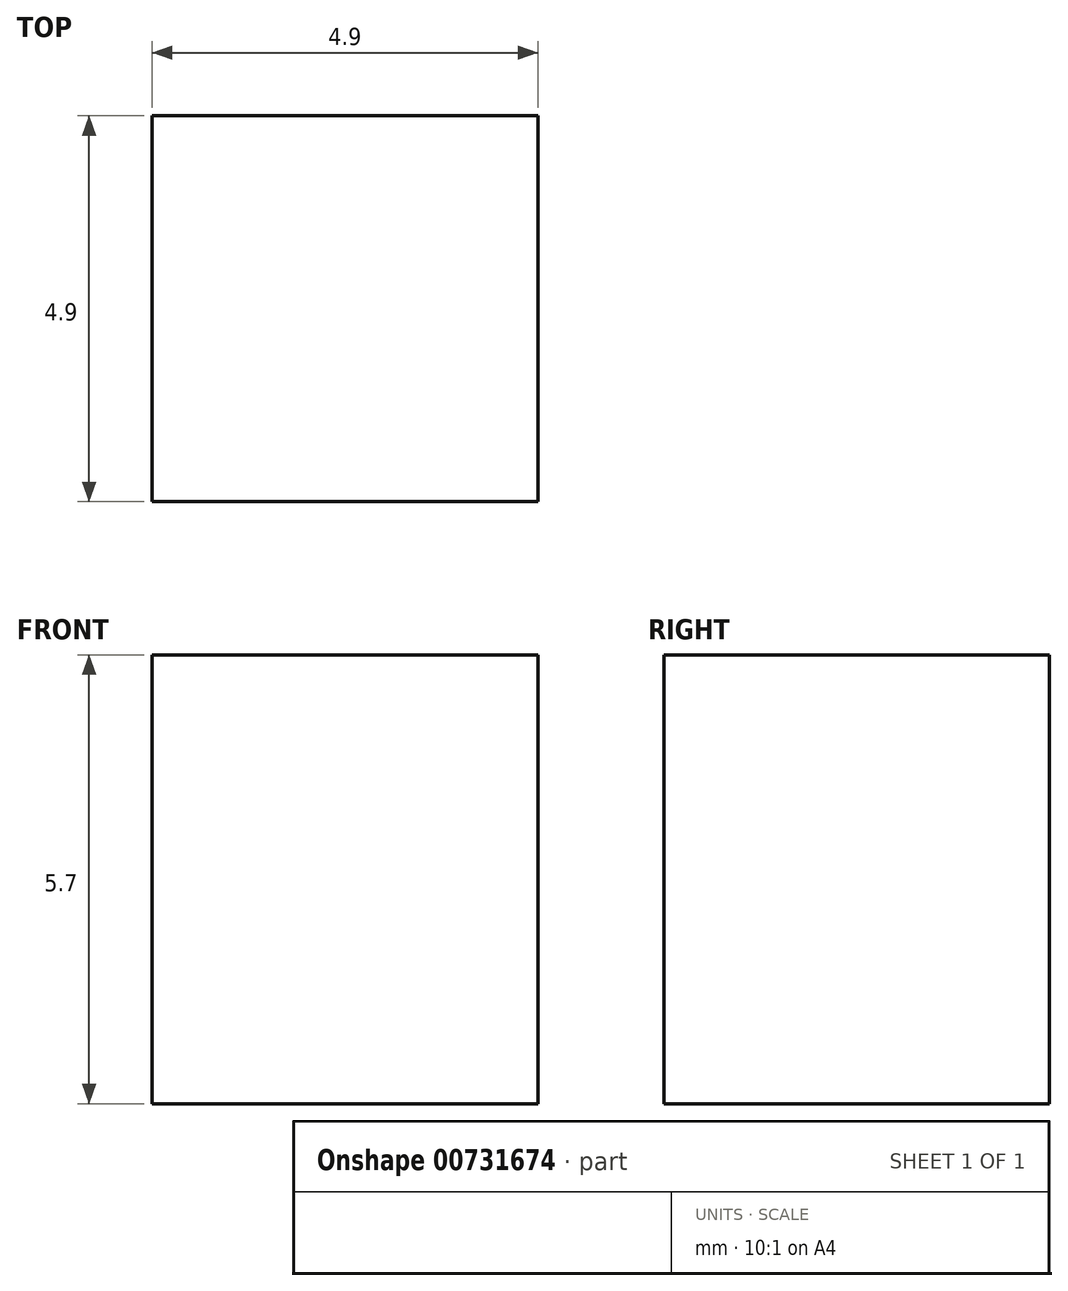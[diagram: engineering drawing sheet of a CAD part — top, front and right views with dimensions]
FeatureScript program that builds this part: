
annotation { "Feature Type Name" : "Feature", "Feature Type Description" : "" }
export const myFeature = defineFeature(function(context is Context, id is Id, definition is map)
    precondition{}
    {
        {
            var Q0;
            Q0=qCreatedBy(makeId("Top.planeOp"),FACE);
            var sketch = newSketch(context, id + "F0", { "sketchPlane" : qUnion([Q0])});
            skLineSegment(sketch, "E0.bottom", {"start": v(-2.45, 2.45) * mm, "end": v(2.45, 2.45) * mm});
            skLineSegment(sketch, "E0.top", {"start": v(-2.45, -2.45) * mm, "end": v(2.45, -2.45) * mm});
            skLineSegment(sketch, "E0.left", {"start": v(-2.45, 2.45) * mm, "end": v(-2.45, -2.45) * mm});
            skLineSegment(sketch, "E0.right", {"start": v(2.45, 2.45) * mm, "end": v(2.45, -2.45) * mm});
            skSolve(sketch);
        }
        {
            var Q0;
            Q0 = qSketchRegion(id + "F0", true);
            extrude(context, id + "F1", {"entities" : qUnion([Q0]), "depth" : 5.7 * mm, "offsetDistance" : 25 * mm});
        }
    });
